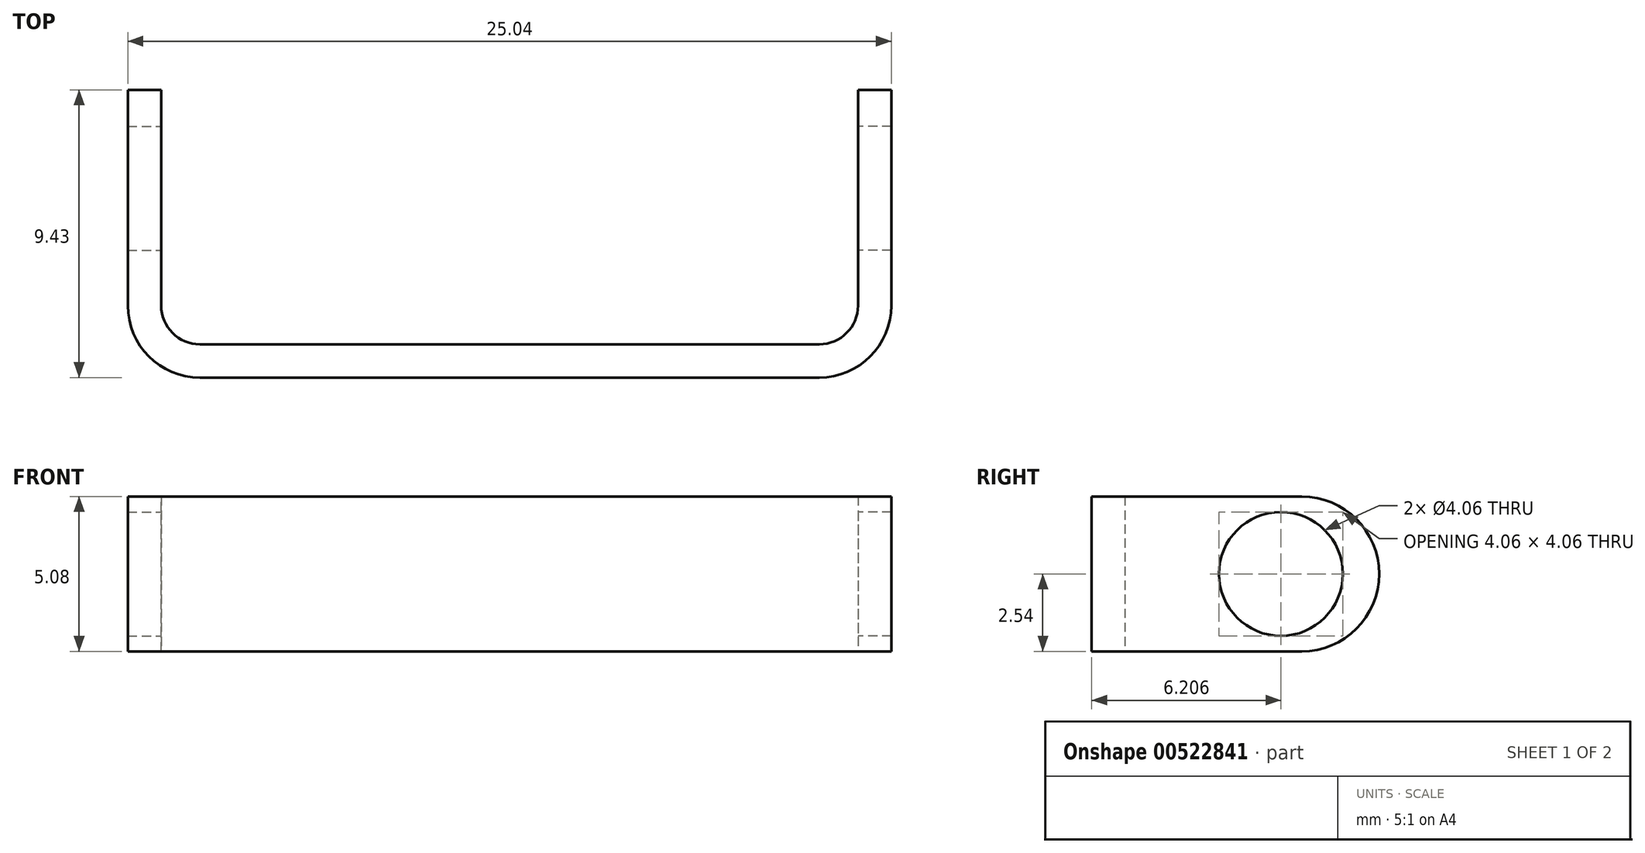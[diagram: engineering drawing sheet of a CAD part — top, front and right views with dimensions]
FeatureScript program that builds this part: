
annotation { "Feature Type Name" : "Feature", "Feature Type Description" : "" }
export const myFeature = defineFeature(function(context is Context, id is Id, definition is map)
    precondition{}
    {
        {
            var Q0;
            Q0=qCreatedBy(makeId("Top.planeOp"),FACE);
            var sketch = newSketch(context, id + "F0", { "sketchPlane" : qUnion([Q0])});
            skLineSegment(sketch, "E0", {"start": v(-12.52, 8.32) * mm, "end": v(-12.52, 2.36) * mm});
            skArc(sketch, "E1", {"start": v(-12.52, 2.36) * mm, "mid": v(-11.83, 0.7) * mm, "end": v(-10.16, 0) * mm});
            skLineSegment(sketch, "E2", {"start": v(-10.16, 0) * mm, "end": v(0, 0) * mm});
            skPoint(sketch, "E3", {"position": v(-12.52, 6.07) * mm});
            skLineSegment(sketch, "E4.0", {"start": v(-10.16, 1.1) * mm, "end": v(0, 1.1) * mm});
            skArc(sketch, "E4.1", {"start": v(-11.43, 2.36) * mm, "mid": v(-11.06, 1.46) * mm, "end": v(-10.16, 1.1) * mm});
            skLineSegment(sketch, "E4.2", {"start": v(-11.43, 8.32) * mm, "end": v(-11.43, 2.36) * mm});
            skLineSegment(sketch, "E5", {"start": v(-12.52, 8.32) * mm, "end": v(-12.52, 9.43) * mm});
            skLineSegment(sketch, "E6", {"start": v(-11.43, 8.32) * mm, "end": v(-11.43, 9.43) * mm});
            skLineSegment(sketch, "E7", {"start": v(-11.43, 9.43) * mm, "end": v(-12.52, 9.43) * mm});
            skLineSegment(sketch, "E8.bottom", {"start": v(0, 1.1) * mm, "end": v(1.22, 1.1) * mm});
            skLineSegment(sketch, "E9.MirrorCS", {"start": v(11.43, 9.43) * mm, "end": v(12.52, 9.43) * mm});
            skArc(sketch, "E10.MirrorCS", {"start": v(11.43, 2.36) * mm, "mid": v(11.06, 1.46) * mm, "end": v(10.16, 1.1) * mm});
            skLineSegment(sketch, "E11.MirrorCS", {"start": v(12.52, 8.32) * mm, "end": v(12.52, 9.43) * mm});
            skLineSegment(sketch, "E12.MirrorCS", {"start": v(11.43, 8.32) * mm, "end": v(11.43, 9.43) * mm});
            skArc(sketch, "E13.MirrorCS", {"start": v(12.52, 2.36) * mm, "mid": v(11.83, 0.7) * mm, "end": v(10.16, 0) * mm});
            skLineSegment(sketch, "E14.MirrorCS", {"start": v(10.16, 0) * mm, "end": v(0, 0) * mm});
            skLineSegment(sketch, "E15.MirrorCS", {"start": v(11.43, 8.32) * mm, "end": v(11.43, 2.36) * mm});
            skLineSegment(sketch, "E16.MirrorCS", {"start": v(12.52, 8.32) * mm, "end": v(12.52, 2.36) * mm});
            skLineSegment(sketch, "E17.MirrorCS", {"start": v(10.16, 1.1) * mm, "end": v(0, 1.1) * mm});
            skPoint(sketch, "E18.MirrorP", {"position": v(12.52, 6.07) * mm});
            skSolve(sketch);
        }
        {
            var Q0;
            Q0 = qSketchRegion(id + "F0", true);
            extrude(context, id + "F1", {"entities" : qUnion([Q0]), "endBound" : BoundingType.SYMMETRIC, "depth" : 5.08 * mm, "offsetDistance" : 25.4 * mm});
        }
        {
            var Q0;
            Q0=makeQuery(id+"F1.opExtrude","CAP_EDGE",EDGE,{"disambiguationData":[OSD([sQuery(id+"F0.wireOp",EDGE,"E7")])],"isStart":false});
            var Q1;
            Q1=makeQuery(id+"F1.opExtrude","CAP_EDGE",EDGE,{"disambiguationData":[OSD([sQuery(id+"F0.wireOp",EDGE,"E7")])],"isStart":true});
            var Q2;
            Q2=makeQuery(id+"F1.opExtrude","CAP_EDGE",EDGE,{"disambiguationData":[OSD([sQuery(id+"F0.wireOp",EDGE,"E9.MirrorCS")])],"isStart":false});
            var Q3;
            Q3=makeQuery(id+"F1.opExtrude","CAP_EDGE",EDGE,{"disambiguationData":[OSD([sQuery(id+"F0.wireOp",EDGE,"E9.MirrorCS")])],"isStart":true});
            fillet(context, id + "F2", {"entities" : qUnion([Q0, Q1, Q2, Q3]), "radius" : 2.54 * mm, "tangentPropagation" : true, "allowEdgeOverflow" : false});
        }
        {
            var Q0;
            Q0=qCreatedBy(makeId("Right.planeOp"),FACE);
            var sketch = newSketch(context, id + "F3", { "sketchPlane" : qUnion([Q0])});
            skPoint(sketch, "E19", {"position": v(6.2, 0) * mm});
            skSolve(sketch);
        }
        {
            var Q0;
            Q0=sQuery(id+"F3.wireOp",VERTEX,"E19");
            var Q1;
            Q1=makeQuery(id+"F1.opExtrude","SWEPT_BODY",BODY,{"disambiguationData":[OSD([sQuery(id+"F0.wireOp",EDGE,"E0"),sQuery(id+"F0.wireOp",EDGE,"E1"),sQuery(id+"F0.wireOp",EDGE,"E2"),sQuery(id+"F0.wireOp",EDGE,"E4.0"),sQuery(id+"F0.wireOp",EDGE,"E4.1"),sQuery(id+"F0.wireOp",EDGE,"E4.2"),sQuery(id+"F0.wireOp",EDGE,"E5"),sQuery(id+"F0.wireOp",EDGE,"E6"),sQuery(id+"F0.wireOp",EDGE,"E7"),sQuery(id+"F0.wireOp",EDGE,"E9.MirrorCS"),sQuery(id+"F0.wireOp",EDGE,"E10.MirrorCS"),sQuery(id+"F0.wireOp",EDGE,"E11.MirrorCS"),sQuery(id+"F0.wireOp",EDGE,"E12.MirrorCS"),sQuery(id+"F0.wireOp",EDGE,"E13.MirrorCS"),sQuery(id+"F0.wireOp",EDGE,"E14.MirrorCS"),sQuery(id+"F0.wireOp",EDGE,"E15.MirrorCS"),sQuery(id+"F0.wireOp",EDGE,"E16.MirrorCS"),sQuery(id+"F0.wireOp",EDGE,"E17.MirrorCS")])]});
            hole(context, id + "F4", {"style" : HoleStyle.SIMPLE, "endStyle" : HoleEndStyle.THROUGH, "oppositeDirection" : true, "holeDiameter" : 4.06 * mm, "isTappedThrough" : true, "tappedDepth" : 12.7 * mm, "tapClearance" : 3, "locations" : qUnion([Q0]), "scope" : qUnion([Q1])});
        }
        {
            var Q0;
            Q0=sQuery(id+"F3.wireOp",VERTEX,"E19");
            var Q1;
            Q1=makeQuery(id+"F1.opExtrude","SWEPT_BODY",BODY,{"disambiguationData":[OSD([sQuery(id+"F0.wireOp",EDGE,"E0"),sQuery(id+"F0.wireOp",EDGE,"E1"),sQuery(id+"F0.wireOp",EDGE,"E2"),sQuery(id+"F0.wireOp",EDGE,"E4.0"),sQuery(id+"F0.wireOp",EDGE,"E4.1"),sQuery(id+"F0.wireOp",EDGE,"E4.2"),sQuery(id+"F0.wireOp",EDGE,"E5"),sQuery(id+"F0.wireOp",EDGE,"E6"),sQuery(id+"F0.wireOp",EDGE,"E7"),sQuery(id+"F0.wireOp",EDGE,"E9.MirrorCS"),sQuery(id+"F0.wireOp",EDGE,"E10.MirrorCS"),sQuery(id+"F0.wireOp",EDGE,"E11.MirrorCS"),sQuery(id+"F0.wireOp",EDGE,"E12.MirrorCS"),sQuery(id+"F0.wireOp",EDGE,"E13.MirrorCS"),sQuery(id+"F0.wireOp",EDGE,"E14.MirrorCS"),sQuery(id+"F0.wireOp",EDGE,"E15.MirrorCS"),sQuery(id+"F0.wireOp",EDGE,"E16.MirrorCS"),sQuery(id+"F0.wireOp",EDGE,"E17.MirrorCS")])]});
            hole(context, id + "F5", {"style" : HoleStyle.SIMPLE, "endStyle" : HoleEndStyle.THROUGH, "holeDiameter" : 4.06 * mm, "isTappedThrough" : true, "tappedDepth" : 12.7 * mm, "tapClearance" : 3, "locations" : qUnion([Q0]), "scope" : qUnion([Q1])});
        }
    });
